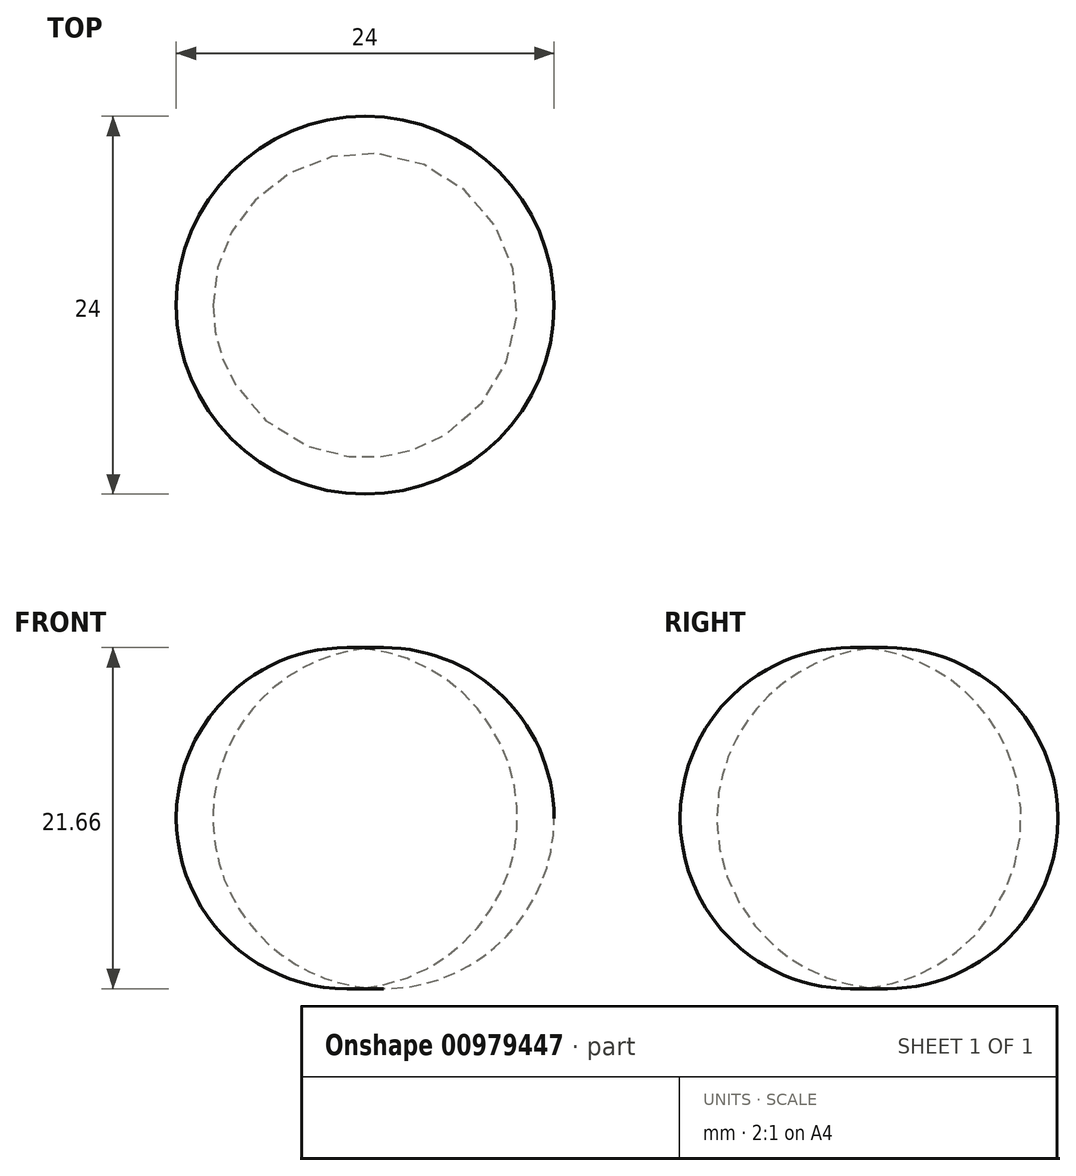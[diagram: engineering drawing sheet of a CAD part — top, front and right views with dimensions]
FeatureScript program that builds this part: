
annotation { "Feature Type Name" : "Feature", "Feature Type Description" : "" }
export const myFeature = defineFeature(function(context is Context, id is Id, definition is map)
    precondition{}
    {
        {
            var Q0;
            Q0=qCreatedBy(makeId("Front.planeOp"),FACE);
            var sketch = newSketch(context, id + "F0", { "sketchPlane" : qUnion([Q0])});
            skArc(sketch, "E0", {"start": v(0, -21.54) * mm, "mid": v(12, -10.77) * mm, "end": v(0, 0) * mm});
            skLineSegment(sketch, "E1", {"start": v(0, 0) * mm, "end": v(0, -21.54) * mm});
            skSolve(sketch);
        }
        {
            var Q0;
            Q0=makeQuery(id+"F0.imprint","IMPRINT",FACE,{"disambiguationData":[TD([[makeQuery(id+"F0.imprint","IMPRINT",EDGE,{"derivedFrom":sQuery(id+"F0.wireOp",EDGE,"E0")}),1.0]])]});
            var Q1;
            Q1=sQuery(id+"F0.wireOp",EDGE,"E1");
            revolve(context, id + "F1", {"surfaceOperationType" : NewSurfaceOperationType.NEW, "entities" : qUnion([Q0]), "axis" : qUnion([Q1]), "revolveType" : RevolveType.ONE_DIRECTION, "angle" : 360 * degree});
        }
    });
